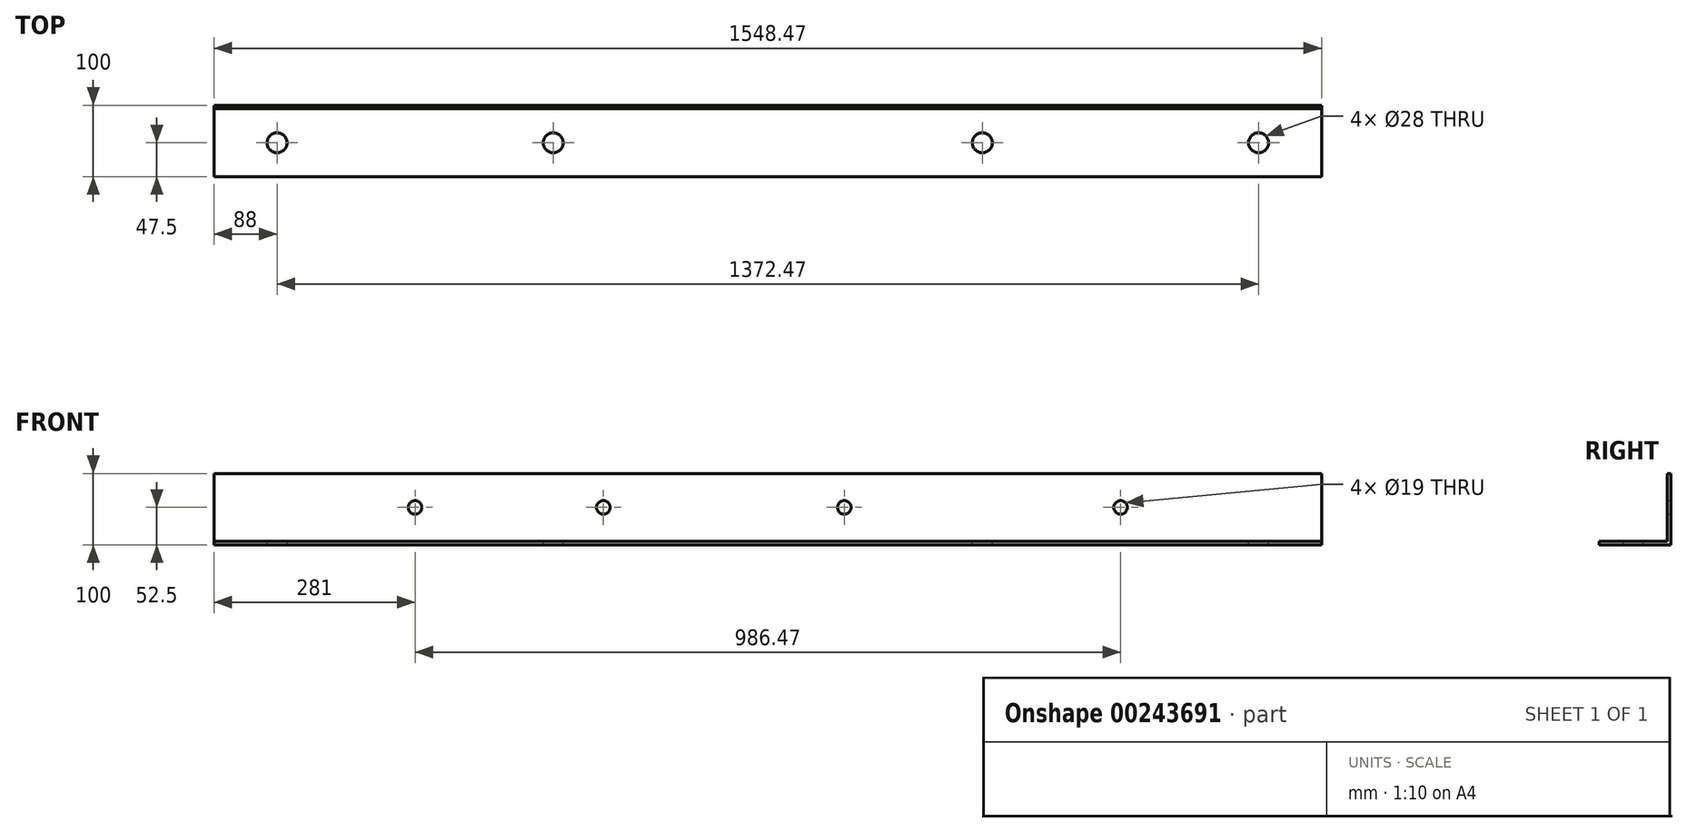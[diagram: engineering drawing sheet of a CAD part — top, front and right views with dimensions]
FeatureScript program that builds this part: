
annotation { "Feature Type Name" : "Feature", "Feature Type Description" : "" }
export const myFeature = defineFeature(function(context is Context, id is Id, definition is map)
    precondition{}
    {
        {
            var Q0;
            Q0=qCreatedBy(makeId("Right.planeOp"),FACE);
            var sketch = newSketch(context, id + "F0", { "sketchPlane" : qUnion([Q0])});
            skLineSegment(sketch, "E0", {"start": v(0, 100) * mm, "end": v(0, 0) * mm});
            skLineSegment(sketch, "E1", {"start": v(0, 0) * mm, "end": v(-100, 0) * mm});
            skLineSegment(sketch, "E2", {"start": v(-100, 0) * mm, "end": v(-100, 5) * mm});
            skLineSegment(sketch, "E3", {"start": v(-100, 5) * mm, "end": v(-5, 5) * mm});
            skLineSegment(sketch, "E4", {"start": v(-5, 5) * mm, "end": v(-5, 100) * mm});
            skLineSegment(sketch, "E5", {"start": v(-5, 100) * mm, "end": v(0, 100) * mm});
            skSolve(sketch);
        }
        {
            var Q0;
            Q0 = qSketchRegion(id + "F0", true);
            extrude(context, id + "F1", {"entities" : qUnion([Q0]), "depth" : 1548.47 * mm});
        }
        {
            var Q0;
            Q0=makeQuery(id+"F1.opExtrude","SWEPT_FACE",FACE,{"disambiguationData":[OSD([sQuery(id+"F0.wireOp",EDGE,"E3")])]});
            var sketch = newSketch(context, id + "F2", { "sketchPlane" : qUnion([Q0])});
            skCircle(sketch, "E6", {"center": v(474.22, -52.5) * mm, "radius": 14 * mm});
            skCircle(sketch, "E7", {"center": v(1074.22, -52.5) * mm, "radius": 14 * mm});
            skCircle(sketch, "E8", {"center": v(1460.47, -52.5) * mm, "radius": 14 * mm});
            skCircle(sketch, "E9", {"center": v(88, -52.5) * mm, "radius": 14 * mm});
            skSolve(sketch);
        }
        {
            var Q0;
            Q0 = qSketchRegion(id + "F2", true);
            var Q1;
            Q1=makeQuery(id+"F1.opExtrude","SWEPT_FACE",FACE,{"disambiguationData":[OSD([sQuery(id+"F0.wireOp",EDGE,"E1")])]});
            extrude(context, id + "F3", {"entities" : qUnion([Q0]), "operationType" : NewBodyOperationType.REMOVE, "endBound" : BoundingType.UP_TO_SURFACE, "oppositeDirection" : true, "endBoundEntityFace" : qUnion([Q1]), "depth" : 25 * mm});
        }
        {
            var Q0;
            Q0=qCreatedBy(makeId("Front.planeOp"),FACE);
            var sketch = newSketch(context, id + "F4", { "sketchPlane" : qUnion([Q0])});
            skCircle(sketch, "E10", {"center": v(281, 52.5) * mm, "radius": 9.5 * mm});
            skCircle(sketch, "E11", {"center": v(544.22, 52.5) * mm, "radius": 9.5 * mm});
            skCircle(sketch, "E12", {"center": v(881.22, 52.5) * mm, "radius": 9.5 * mm});
            skCircle(sketch, "E13", {"center": v(1267.47, 52.5) * mm, "radius": 9.5 * mm});
            skSolve(sketch);
        }
        {
            var Q0;
            Q0=makeQuery(id+"F4.imprint","IMPRINT",FACE,{"disambiguationData":[TD([[makeQuery(id+"F4.imprint","IMPRINT",EDGE,{"derivedFrom":sQuery(id+"F4.wireOp",EDGE,"E13")}),1.0]])]});
            var Q1;
            Q1=makeQuery(id+"F4.imprint","IMPRINT",FACE,{"disambiguationData":[TD([[makeQuery(id+"F4.imprint","IMPRINT",EDGE,{"derivedFrom":sQuery(id+"F4.wireOp",EDGE,"E12")}),1.0]])]});
            var Q2;
            Q2=makeQuery(id+"F4.imprint","IMPRINT",FACE,{"disambiguationData":[TD([[makeQuery(id+"F4.imprint","IMPRINT",EDGE,{"derivedFrom":sQuery(id+"F4.wireOp",EDGE,"E11")}),1.0]])]});
            var Q3;
            Q3=makeQuery(id+"F4.imprint","IMPRINT",FACE,{"disambiguationData":[TD([[makeQuery(id+"F4.imprint","IMPRINT",EDGE,{"derivedFrom":sQuery(id+"F4.wireOp",EDGE,"E10")}),1.0]])]});
            var Q4;
            Q4=makeQuery(id+"F1.opExtrude","SWEPT_FACE",FACE,{"disambiguationData":[OSD([sQuery(id+"F0.wireOp",EDGE,"E4")])]});
            extrude(context, id + "F5", {"entities" : qUnion([Q0, Q1, Q2, Q3]), "operationType" : NewBodyOperationType.REMOVE, "endBound" : BoundingType.UP_TO_SURFACE, "endBoundEntityFace" : qUnion([Q4]), "depth" : 25 * mm});
        }
    });
